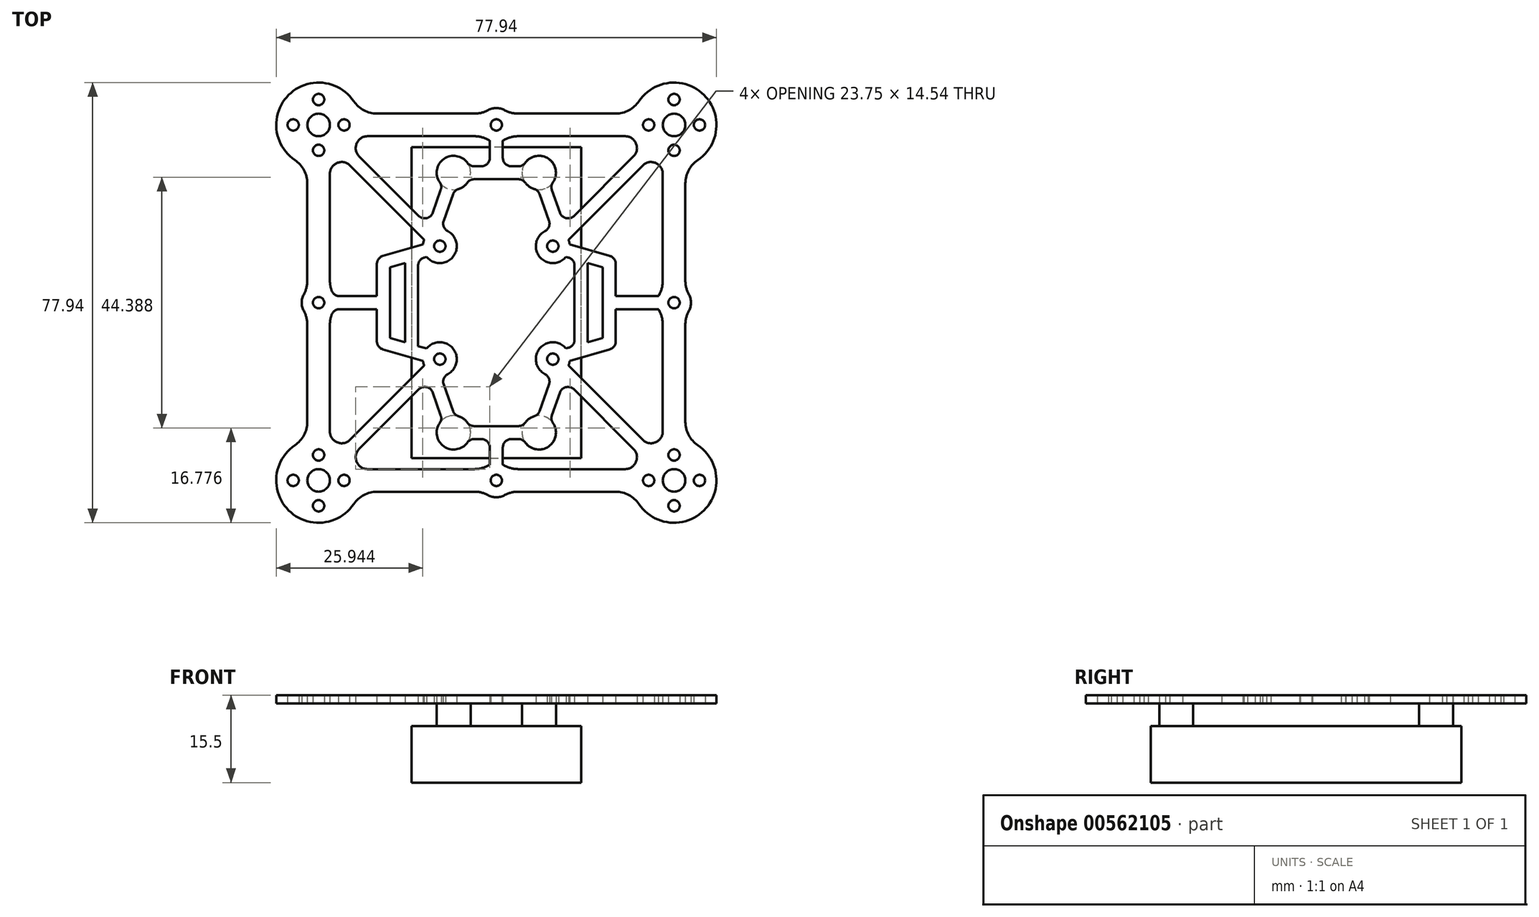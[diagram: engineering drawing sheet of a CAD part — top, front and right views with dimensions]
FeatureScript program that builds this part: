
annotation { "Feature Type Name" : "Feature", "Feature Type Description" : "" }
export const myFeature = defineFeature(function(context is Context, id is Id, definition is map)
    precondition{}
    {
        {
            var Q0;
            Q0=qCreatedBy(makeId("Top.planeOp"),FACE);
            var sketch = newSketch(context, id + "F0", { "sketchPlane" : qUnion([Q0])});
            skLineSegment(sketch, "E0.bottom", {"start": v(15, -27.5) * mm, "end": v(-15, -27.5) * mm});
            skLineSegment(sketch, "E0.top", {"start": v(15, 27.5) * mm, "end": v(-15, 27.5) * mm});
            skLineSegment(sketch, "E0.left", {"start": v(15, -27.5) * mm, "end": v(15, 27.5) * mm});
            skLineSegment(sketch, "E0.right", {"start": v(-15, -27.5) * mm, "end": v(-15, 27.5) * mm});
            skPoint(sketch, "E0.middle", {"position": v(0, 0) * mm});
            skSolve(sketch);
        }
        {
            var Q0;
            Q0=qCreatedBy(makeId("Top.planeOp"),FACE);
            var sketch = newSketch(context, id + "F1", { "sketchPlane" : qUnion([Q0])});
            skCircle(sketch, "E1", {"center": v(0, 0) * mm, "radius": 44.5 * mm, "construction": true});
            skLineSegment(sketch, "E2.bottom", {"start": v(31.47, -31.47) * mm, "end": v(-31.47, -31.47) * mm, "construction": true});
            skLineSegment(sketch, "E2.top", {"start": v(31.47, 31.47) * mm, "end": v(-31.47, 31.47) * mm, "construction": true});
            skLineSegment(sketch, "E2.left", {"start": v(31.47, -31.47) * mm, "end": v(31.47, 31.47) * mm, "construction": true});
            skLineSegment(sketch, "E2.right", {"start": v(-31.47, -31.47) * mm, "end": v(-31.47, 31.47) * mm, "construction": true});
            skCircle(sketch, "E3", {"center": v(-31.47, 31.47) * mm, "radius": 2 * mm});
            skCircle(sketch, "E4", {"center": v(31.47, 31.47) * mm, "radius": 2 * mm});
            skCircle(sketch, "E5", {"center": v(31.47, -31.47) * mm, "radius": 2 * mm});
            skCircle(sketch, "E6", {"center": v(-31.47, -31.47) * mm, "radius": 2 * mm});
            skCircle(sketch, "E7", {"center": v(-31.47, 0) * mm, "radius": 1 * mm});
            skCircle(sketch, "E8", {"center": v(0, 31.47) * mm, "radius": 1 * mm});
            skCircle(sketch, "E9", {"center": v(31.47, 0) * mm, "radius": 1 * mm});
            skCircle(sketch, "E10", {"center": v(0, -31.47) * mm, "radius": 1 * mm});
            skArc(sketch, "E11", {"start": v(-28.3, 24.66) * mm, "mid": v(-28.26, 24.68) * mm, "end": v(-28.22, 24.7) * mm});
            skArc(sketch, "E12", {"start": v(24.66, 28.3) * mm, "mid": v(24.68, 28.26) * mm, "end": v(24.7, 28.22) * mm});
            skArc(sketch, "E13", {"start": v(28.3, -24.66) * mm, "mid": v(28.26, -24.68) * mm, "end": v(28.22, -24.7) * mm});
            skArc(sketch, "E14", {"start": v(-35.67, -25.25) * mm, "mid": v(-36.77, -36.77) * mm, "end": v(-25.25, -35.67) * mm});
            skLineSegment(sketch, "E15.bottom", {"start": v(22.85, -29.47) * mm, "end": v(3.87, -29.47) * mm});
            skLineSegment(sketch, "E15.top", {"start": v(22.85, 29.47) * mm, "end": v(3.87, 29.47) * mm});
            skLineSegment(sketch, "E15.left", {"start": v(29.47, -22.85) * mm, "end": v(29.47, -3.87) * mm});
            skLineSegment(sketch, "E15.right", {"start": v(-29.47, -22.85) * mm, "end": v(-29.47, -3.87) * mm});
            skLineSegment(sketch, "E16.bottom", {"start": v(10, -10) * mm, "end": v(-10, -10) * mm, "construction": true});
            skLineSegment(sketch, "E16.top", {"start": v(10, 10) * mm, "end": v(-10, 10) * mm, "construction": true});
            skLineSegment(sketch, "E16.left", {"start": v(10, -10) * mm, "end": v(10, 10) * mm, "construction": true});
            skLineSegment(sketch, "E16.right", {"start": v(-10, -10) * mm, "end": v(-10, 10) * mm, "construction": true});
            skCircle(sketch, "E17", {"center": v(-10, 10) * mm, "radius": 1 * mm});
            skCircle(sketch, "E18", {"center": v(10, 10) * mm, "radius": 1 * mm});
            skCircle(sketch, "E19", {"center": v(10, -10) * mm, "radius": 1 * mm});
            skCircle(sketch, "E20", {"center": v(-10, -10) * mm, "radius": 1 * mm});
            skLineSegment(sketch, "E21", {"start": v(-31.47, 0) * mm, "end": v(31.47, 0) * mm, "construction": true});
            skLineSegment(sketch, "E22", {"start": v(0, 31.47) * mm, "end": v(0, -31.47) * mm, "construction": true});
            skLineSegment(sketch, "E23.trimOffspring", {"start": v(-33.47, -21.11) * mm, "end": v(-33.47, -3.87) * mm});
            skLineSegment(sketch, "E24.trimOffspring", {"start": v(21.11, 33.47) * mm, "end": v(3.87, 33.47) * mm});
            skLineSegment(sketch, "E25.trimOffspring", {"start": v(21.11, -33.47) * mm, "end": v(3.87, -33.47) * mm});
            skLineSegment(sketch, "E26.trimOffspring", {"start": v(33.47, -21.11) * mm, "end": v(33.47, -3.87) * mm});
            skArc(sketch, "E27.trimOffspring", {"start": v(-25.25, 35.67) * mm, "mid": v(-36.77, 36.77) * mm, "end": v(-35.67, 25.25) * mm});
            skArc(sketch, "E28.trimOffspring", {"start": v(35.67, 25.25) * mm, "mid": v(36.77, 36.77) * mm, "end": v(25.25, 35.67) * mm});
            skArc(sketch, "E29.trimOffspring", {"start": v(25.25, -35.67) * mm, "mid": v(36.77, -36.77) * mm, "end": v(35.67, -25.25) * mm});
            skArc(sketch, "E30.trimOffspring", {"start": v(-24.66, -28.3) * mm, "mid": v(-24.68, -28.26) * mm, "end": v(-24.7, -28.22) * mm});
            skCircle(sketch, "E31", {"center": v(-31.47, 31.47) * mm, "radius": 4.5 * mm, "construction": true});
            skCircle(sketch, "E32", {"center": v(31.47, 31.47) * mm, "radius": 4.5 * mm, "construction": true});
            skCircle(sketch, "E33", {"center": v(31.47, -31.47) * mm, "radius": 4.5 * mm, "construction": true});
            skCircle(sketch, "E34", {"center": v(-31.47, -31.47) * mm, "radius": 4.5 * mm, "construction": true});
            skCircle(sketch, "E35", {"center": v(-26.97, 31.47) * mm, "radius": 1 * mm});
            skCircle(sketch, "E36", {"center": v(-35.97, 31.47) * mm, "radius": 1 * mm});
            skCircle(sketch, "E37", {"center": v(-31.47, 26.97) * mm, "radius": 1 * mm});
            skCircle(sketch, "E38", {"center": v(-31.47, 35.97) * mm, "radius": 1 * mm});
            skCircle(sketch, "E39", {"center": v(26.97, 31.47) * mm, "radius": 1 * mm});
            skCircle(sketch, "E40", {"center": v(31.47, 26.97) * mm, "radius": 1 * mm});
            skCircle(sketch, "E41", {"center": v(31.47, 35.97) * mm, "radius": 1 * mm});
            skCircle(sketch, "E42", {"center": v(35.97, 31.47) * mm, "radius": 1 * mm});
            skCircle(sketch, "E43", {"center": v(31.47, -26.97) * mm, "radius": 1 * mm});
            skCircle(sketch, "E44", {"center": v(26.97, -31.47) * mm, "radius": 1 * mm});
            skCircle(sketch, "E45", {"center": v(35.97, -31.47) * mm, "radius": 1 * mm});
            skCircle(sketch, "E46", {"center": v(31.47, -35.97) * mm, "radius": 1 * mm});
            skCircle(sketch, "E47", {"center": v(-31.47, -26.97) * mm, "radius": 1 * mm});
            skCircle(sketch, "E48", {"center": v(-26.97, -31.47) * mm, "radius": 1 * mm});
            skCircle(sketch, "E49", {"center": v(-31.47, -35.97) * mm, "radius": 1 * mm});
            skCircle(sketch, "E50", {"center": v(-35.97, -31.47) * mm, "radius": 1 * mm});
            skArc(sketch, "E51", {"start": v(-1.45, 28.84) * mm, "mid": v(-1.3, 28.76) * mm, "end": v(-1.15, 28.7) * mm});
            skArc(sketch, "E52", {"start": v(-34.1, 1.45) * mm, "mid": v(-34.47, 0) * mm, "end": v(-34.1, -1.45) * mm});
            skArc(sketch, "E53", {"start": v(28.84, 1.45) * mm, "mid": v(28.76, 1.3) * mm, "end": v(28.7, 1.15) * mm});
            skArc(sketch, "E54", {"start": v(-1.45, -34.1) * mm, "mid": v(0, -34.47) * mm, "end": v(1.45, -34.1) * mm});
            skLineSegment(sketch, "E55.trimOffspring", {"start": v(-3.87, 33.47) * mm, "end": v(-21.11, 33.47) * mm});
            skLineSegment(sketch, "E56.trimOffspring", {"start": v(-3.87, 29.47) * mm, "end": v(-22.85, 29.47) * mm});
            skArc(sketch, "E57.trimOffspring", {"start": v(1.45, 34.1) * mm, "mid": v(0, 34.47) * mm, "end": v(-1.45, 34.1) * mm});
            skLineSegment(sketch, "E58.trimOffspring", {"start": v(-33.47, 3.87) * mm, "end": v(-33.47, 21.11) * mm});
            skLineSegment(sketch, "E59.trimOffspring", {"start": v(-29.47, 3.87) * mm, "end": v(-29.47, 22.85) * mm});
            skLineSegment(sketch, "E60.trimOffspring", {"start": v(-3.87, -29.47) * mm, "end": v(-22.85, -29.47) * mm});
            skArc(sketch, "E61.trimOffspring", {"start": v(1.45, -28.84) * mm, "mid": v(1.3, -28.76) * mm, "end": v(1.15, -28.7) * mm});
            skLineSegment(sketch, "E62.trimOffspring", {"start": v(-3.87, -33.47) * mm, "end": v(-21.11, -33.47) * mm});
            skLineSegment(sketch, "E63.trimOffspring", {"start": v(33.47, 3.87) * mm, "end": v(33.47, 21.11) * mm});
            skLineSegment(sketch, "E64.trimOffspring", {"start": v(29.47, 3.87) * mm, "end": v(29.47, 22.85) * mm});
            skArc(sketch, "E65.trimOffspring", {"start": v(34.1, -1.45) * mm, "mid": v(34.47, 0) * mm, "end": v(34.1, 1.45) * mm});
            skLineSegment(sketch, "E66", {"start": v(-31.47, -31.47) * mm, "end": v(31.47, 31.47) * mm, "construction": true});
            skLineSegment(sketch, "E67", {"start": v(-31.47, 31.47) * mm, "end": v(31.47, -31.47) * mm, "construction": true});
            skArc(sketch, "E68", {"start": v(-12.77, 11.15) * mm, "mid": v(-12.9, 10.75) * mm, "end": v(-12.98, 10.33) * mm});
            skArc(sketch, "E69", {"start": v(8.6, 12.66) * mm, "mid": v(7.68, 8.1) * mm, "end": v(12.34, 8.12) * mm});
            skArc(sketch, "E70", {"start": v(12.77, -11.15) * mm, "mid": v(12.9, -10.75) * mm, "end": v(12.98, -10.33) * mm});
            skArc(sketch, "E71", {"start": v(-8.6, -12.66) * mm, "mid": v(-7.68, -8.1) * mm, "end": v(-12.34, -8.12) * mm});
            skLineSegment(sketch, "E72", {"start": v(-25.94, 24.32) * mm, "end": v(-12.77, 11.15) * mm});
            skLineSegment(sketch, "E73", {"start": v(-24.32, 25.94) * mm, "end": v(-13.73, 15.36) * mm});
            skLineSegment(sketch, "E74", {"start": v(24.32, 25.94) * mm, "end": v(13.73, 15.36) * mm});
            skLineSegment(sketch, "E75", {"start": v(25.94, 24.32) * mm, "end": v(12.77, 11.15) * mm});
            skLineSegment(sketch, "E76", {"start": v(25.94, -24.32) * mm, "end": v(12.77, -11.15) * mm});
            skLineSegment(sketch, "E77", {"start": v(13.73, -15.36) * mm, "end": v(24.32, -25.94) * mm});
            skLineSegment(sketch, "E78", {"start": v(-13.73, -15.36) * mm, "end": v(-24.32, -25.94) * mm});
            skLineSegment(sketch, "E79", {"start": v(-12.77, -11.15) * mm, "end": v(-25.94, -24.32) * mm});
            skPoint(sketch, "E80.visualSharp", {"position": v(-33.47, 24.24) * mm});
            skArc(sketch, "E80.filletArc", {"start": v(-33.47, 21.11) * mm, "mid": v(-34.05, 23.46) * mm, "end": v(-35.67, 25.25) * mm});
            skPoint(sketch, "E81.visualSharp", {"position": v(-24.24, 33.47) * mm});
            skArc(sketch, "E81.filletArc", {"start": v(-25.25, 35.67) * mm, "mid": v(-23.46, 34.05) * mm, "end": v(-21.11, 33.47) * mm});
            skPoint(sketch, "E82.visualSharp", {"position": v(24.24, 33.47) * mm});
            skArc(sketch, "E82.filletArc", {"start": v(21.11, 33.47) * mm, "mid": v(23.46, 34.05) * mm, "end": v(25.25, 35.67) * mm});
            skPoint(sketch, "E83.visualSharp", {"position": v(33.47, 24.24) * mm});
            skArc(sketch, "E83.filletArc", {"start": v(35.67, 25.25) * mm, "mid": v(34.05, 23.46) * mm, "end": v(33.47, 21.11) * mm});
            skPoint(sketch, "E84.visualSharp", {"position": v(33.47, -24.24) * mm});
            skArc(sketch, "E84.filletArc", {"start": v(33.47, -21.11) * mm, "mid": v(34.05, -23.46) * mm, "end": v(35.67, -25.25) * mm});
            skPoint(sketch, "E85.visualSharp", {"position": v(24.24, -33.47) * mm});
            skArc(sketch, "E85.filletArc", {"start": v(25.25, -35.67) * mm, "mid": v(23.46, -34.05) * mm, "end": v(21.11, -33.47) * mm});
            skPoint(sketch, "E86.visualSharp", {"position": v(-33.47, -24.24) * mm});
            skArc(sketch, "E86.filletArc", {"start": v(-35.67, -25.25) * mm, "mid": v(-34.05, -23.46) * mm, "end": v(-33.47, -21.11) * mm});
            skPoint(sketch, "E87.visualSharp", {"position": v(-24.24, -33.47) * mm});
            skArc(sketch, "E87.filletArc", {"start": v(-21.11, -33.47) * mm, "mid": v(-23.46, -34.05) * mm, "end": v(-25.25, -35.67) * mm});
            skPoint(sketch, "E88.visualSharp", {"position": v(-33.47, 2.24) * mm});
            skArc(sketch, "E88.filletArc", {"start": v(-34.1, 1.45) * mm, "mid": v(-33.63, 2.62) * mm, "end": v(-33.47, 3.87) * mm});
            skPoint(sketch, "E89.visualSharp", {"position": v(-33.47, -2.24) * mm});
            skArc(sketch, "E89.filletArc", {"start": v(-33.47, -3.87) * mm, "mid": v(-33.63, -2.62) * mm, "end": v(-34.1, -1.45) * mm});
            skArc(sketch, "E90.filletArc", {"start": v(-29.15, -2.13) * mm, "mid": v(-29.39, -2.99) * mm, "end": v(-29.47, -3.87) * mm});
            skArc(sketch, "E91.filletArc", {"start": v(-29.47, 3.87) * mm, "mid": v(-29.39, 2.99) * mm, "end": v(-29.15, 2.13) * mm});
            skPoint(sketch, "E92.visualSharp", {"position": v(-2.24, 29.47) * mm});
            skArc(sketch, "E92.filletArc", {"start": v(-1.45, 28.84) * mm, "mid": v(-2.62, 29.3) * mm, "end": v(-3.87, 29.47) * mm});
            skPoint(sketch, "E93.visualSharp", {"position": v(2.24, 29.47) * mm});
            skArc(sketch, "E93.filletArc", {"start": v(3.87, 29.47) * mm, "mid": v(2.62, 29.3) * mm, "end": v(1.45, 28.84) * mm});
            skPoint(sketch, "E94.visualSharp", {"position": v(2.24, 33.47) * mm});
            skArc(sketch, "E94.filletArc", {"start": v(1.45, 34.1) * mm, "mid": v(2.62, 33.63) * mm, "end": v(3.87, 33.47) * mm});
            skPoint(sketch, "E95.visualSharp", {"position": v(-2.24, 33.47) * mm});
            skArc(sketch, "E95.filletArc", {"start": v(-3.87, 33.47) * mm, "mid": v(-2.62, 33.63) * mm, "end": v(-1.45, 34.1) * mm});
            skPoint(sketch, "E96.visualSharp", {"position": v(29.47, 2.24) * mm});
            skArc(sketch, "E96.filletArc", {"start": v(28.84, 1.45) * mm, "mid": v(29.3, 2.62) * mm, "end": v(29.47, 3.87) * mm});
            skPoint(sketch, "E97.visualSharp", {"position": v(29.47, -2.24) * mm});
            skArc(sketch, "E97.filletArc", {"start": v(29.47, -3.87) * mm, "mid": v(29.3, -2.62) * mm, "end": v(28.84, -1.45) * mm});
            skPoint(sketch, "E98.visualSharp", {"position": v(33.47, -2.24) * mm});
            skArc(sketch, "E98.filletArc", {"start": v(34.1, -1.45) * mm, "mid": v(33.63, -2.62) * mm, "end": v(33.47, -3.87) * mm});
            skPoint(sketch, "E99.visualSharp", {"position": v(33.47, 2.24) * mm});
            skArc(sketch, "E99.filletArc", {"start": v(33.47, 3.87) * mm, "mid": v(33.63, 2.62) * mm, "end": v(34.1, 1.45) * mm});
            skPoint(sketch, "E100.visualSharp", {"position": v(2.24, -33.47) * mm});
            skArc(sketch, "E100.filletArc", {"start": v(3.87, -33.47) * mm, "mid": v(2.62, -33.63) * mm, "end": v(1.45, -34.1) * mm});
            skPoint(sketch, "E101.visualSharp", {"position": v(-2.24, -33.47) * mm});
            skArc(sketch, "E101.filletArc", {"start": v(-1.45, -34.1) * mm, "mid": v(-2.62, -33.63) * mm, "end": v(-3.87, -33.47) * mm});
            skPoint(sketch, "E102.visualSharp", {"position": v(-2.24, -29.47) * mm});
            skArc(sketch, "E102.filletArc", {"start": v(-3.87, -29.47) * mm, "mid": v(-2.62, -29.3) * mm, "end": v(-1.45, -28.84) * mm});
            skPoint(sketch, "E103.visualSharp", {"position": v(2.24, -29.47) * mm});
            skArc(sketch, "E103.filletArc", {"start": v(1.45, -28.84) * mm, "mid": v(2.62, -29.3) * mm, "end": v(3.87, -29.47) * mm});
            skArc(sketch, "E104.trimOffspring", {"start": v(-24.7, 28.22) * mm, "mid": v(-24.68, 28.26) * mm, "end": v(-24.66, 28.3) * mm});
            skArc(sketch, "E105.trimOffspring", {"start": v(28.22, 24.7) * mm, "mid": v(28.26, 24.68) * mm, "end": v(28.3, 24.66) * mm});
            skArc(sketch, "E106.trimOffspring", {"start": v(-28.22, -24.7) * mm, "mid": v(-28.26, -24.68) * mm, "end": v(-28.3, -24.66) * mm});
            skArc(sketch, "E107.trimOffspring", {"start": v(24.7, -28.22) * mm, "mid": v(24.68, -28.26) * mm, "end": v(24.66, -28.3) * mm});
            skPoint(sketch, "E108.visualSharp", {"position": v(-29.47, 24.24) * mm});
            skArc(sketch, "E108.filletArc", {"start": v(-28.3, 24.66) * mm, "mid": v(-29.15, 23.93) * mm, "end": v(-29.47, 22.85) * mm});
            skPoint(sketch, "E109.visualSharp", {"position": v(-27.04, 25.41) * mm});
            skArc(sketch, "E109.filletArc", {"start": v(-25.94, 24.32) * mm, "mid": v(-27.02, 24.87) * mm, "end": v(-28.22, 24.7) * mm});
            skPoint(sketch, "E110.visualSharp", {"position": v(-24.24, 29.47) * mm});
            skArc(sketch, "E110.filletArc", {"start": v(-22.85, 29.47) * mm, "mid": v(-23.93, 29.15) * mm, "end": v(-24.66, 28.3) * mm});
            skPoint(sketch, "E111.visualSharp", {"position": v(-25.41, 27.04) * mm});
            skArc(sketch, "E111.filletArc", {"start": v(-24.7, 28.22) * mm, "mid": v(-24.87, 27.02) * mm, "end": v(-24.32, 25.94) * mm});
            skPoint(sketch, "E112.visualSharp", {"position": v(24.24, 29.47) * mm});
            skArc(sketch, "E112.filletArc", {"start": v(24.66, 28.3) * mm, "mid": v(23.93, 29.15) * mm, "end": v(22.85, 29.47) * mm});
            skPoint(sketch, "E113.visualSharp", {"position": v(25.41, 27.04) * mm});
            skArc(sketch, "E113.filletArc", {"start": v(24.32, 25.94) * mm, "mid": v(24.87, 27.02) * mm, "end": v(24.7, 28.22) * mm});
            skPoint(sketch, "E114.visualSharp", {"position": v(27.04, 25.41) * mm});
            skArc(sketch, "E114.filletArc", {"start": v(28.22, 24.7) * mm, "mid": v(27.02, 24.87) * mm, "end": v(25.94, 24.32) * mm});
            skPoint(sketch, "E115.visualSharp", {"position": v(29.47, 24.24) * mm});
            skArc(sketch, "E115.filletArc", {"start": v(29.47, 22.85) * mm, "mid": v(29.15, 23.93) * mm, "end": v(28.3, 24.66) * mm});
            skPoint(sketch, "E116.visualSharp", {"position": v(29.47, -24.24) * mm});
            skArc(sketch, "E116.filletArc", {"start": v(28.3, -24.66) * mm, "mid": v(29.15, -23.93) * mm, "end": v(29.47, -22.85) * mm});
            skPoint(sketch, "E117.visualSharp", {"position": v(27.04, -25.41) * mm});
            skArc(sketch, "E117.filletArc", {"start": v(25.94, -24.32) * mm, "mid": v(27.02, -24.87) * mm, "end": v(28.22, -24.7) * mm});
            skPoint(sketch, "E118.visualSharp", {"position": v(25.41, -27.04) * mm});
            skArc(sketch, "E118.filletArc", {"start": v(24.7, -28.22) * mm, "mid": v(24.87, -27.02) * mm, "end": v(24.32, -25.94) * mm});
            skPoint(sketch, "E119.visualSharp", {"position": v(24.24, -29.47) * mm});
            skArc(sketch, "E119.filletArc", {"start": v(22.85, -29.47) * mm, "mid": v(23.93, -29.15) * mm, "end": v(24.66, -28.3) * mm});
            skPoint(sketch, "E120.visualSharp", {"position": v(-24.24, -29.47) * mm});
            skArc(sketch, "E120.filletArc", {"start": v(-24.66, -28.3) * mm, "mid": v(-23.93, -29.15) * mm, "end": v(-22.85, -29.47) * mm});
            skPoint(sketch, "E121.visualSharp", {"position": v(-25.41, -27.04) * mm});
            skArc(sketch, "E121.filletArc", {"start": v(-24.32, -25.94) * mm, "mid": v(-24.87, -27.02) * mm, "end": v(-24.7, -28.22) * mm});
            skPoint(sketch, "E122.visualSharp", {"position": v(-27.04, -25.41) * mm});
            skArc(sketch, "E122.filletArc", {"start": v(-28.22, -24.7) * mm, "mid": v(-27.02, -24.87) * mm, "end": v(-25.94, -24.32) * mm});
            skPoint(sketch, "E123.visualSharp", {"position": v(-29.47, -24.24) * mm});
            skArc(sketch, "E123.filletArc", {"start": v(-29.47, -22.85) * mm, "mid": v(-29.15, -23.93) * mm, "end": v(-28.3, -24.66) * mm});
            skLineSegment(sketch, "E124", {"start": v(-12.88, 9.16) * mm, "end": v(-20, 7.1) * mm, "construction": true});
            skLineSegment(sketch, "E125", {"start": v(-20, 7.1) * mm, "end": v(-20, -7.1) * mm, "construction": true});
            skLineSegment(sketch, "E126", {"start": v(-20, -7.1) * mm, "end": v(-12.88, -9.16) * mm, "construction": true});
            skLineSegment(sketch, "E127", {"start": v(20, 7.1) * mm, "end": v(20, -7.1) * mm, "construction": true});
            skLineSegment(sketch, "E128", {"start": v(-11.15, 12.77) * mm, "end": v(-7.55, 23) * mm, "construction": true});
            skLineSegment(sketch, "E129", {"start": v(-7.55, 23) * mm, "end": v(7.55, 23) * mm, "construction": true});
            skLineSegment(sketch, "E130", {"start": v(7.55, 23) * mm, "end": v(11.15, 12.77) * mm, "construction": true});
            skLineSegment(sketch, "E131", {"start": v(-11.15, -12.77) * mm, "end": v(-7.55, -23) * mm, "construction": true});
            skLineSegment(sketch, "E132", {"start": v(-7.55, -23) * mm, "end": v(7.55, -23) * mm, "construction": true});
            skLineSegment(sketch, "E133", {"start": v(7.55, -23) * mm, "end": v(11.15, -12.77) * mm, "construction": true});
            skPoint(sketch, "E134", {"position": v(0, 23) * mm});
            skPoint(sketch, "E135", {"position": v(0, -23) * mm});
            skPoint(sketch, "E136", {"position": v(-20, 0) * mm});
            skPoint(sketch, "E137", {"position": v(20, 0) * mm});
            skPoint(sketch, "E138", {"position": v(0, -44.5) * mm});
            skPoint(sketch, "E139", {"position": v(-44.5, 0) * mm});
            skLineSegment(sketch, "E140", {"start": v(20, 7.1) * mm, "end": v(12.88, 9.16) * mm, "construction": true});
            skLineSegment(sketch, "E141", {"start": v(20, -7.1) * mm, "end": v(12.88, -9.16) * mm, "construction": true});
            skArc(sketch, "E142", {"start": v(-6.69, 20.13) * mm, "mid": v(-5.82, 20.55) * mm, "end": v(-5.13, 21.23) * mm});
            skArc(sketch, "E143", {"start": v(-10.02, -21.3) * mm, "mid": v(-9.29, -25.45) * mm, "end": v(-5.13, -24.77) * mm});
            skArc(sketch, "E144", {"start": v(5.13, -24.77) * mm, "mid": v(9.29, -25.45) * mm, "end": v(10.02, -21.3) * mm});
            skLineSegment(sketch, "E145", {"start": v(-9.84, 19.95) * mm, "end": v(-11.26, 15.92) * mm});
            skLineSegment(sketch, "E146", {"start": v(-7.67, 19.19) * mm, "end": v(-9.33, 14.48) * mm});
            skLineSegment(sketch, "E147", {"start": v(7.67, 19.19) * mm, "end": v(9.33, 14.48) * mm});
            skLineSegment(sketch, "E148", {"start": v(9.84, 19.95) * mm, "end": v(11.26, 15.92) * mm});
            skLineSegment(sketch, "E149", {"start": v(11.26, -15.92) * mm, "end": v(9.84, -19.95) * mm});
            skLineSegment(sketch, "E150", {"start": v(9.33, -14.48) * mm, "end": v(7.67, -19.19) * mm});
            skLineSegment(sketch, "E151", {"start": v(3.92, -21.85) * mm, "end": v(-3.92, -21.85) * mm});
            skLineSegment(sketch, "E152", {"start": v(-3.92, -24.15) * mm, "end": v(-2.65, -24.15) * mm});
            skLineSegment(sketch, "E153", {"start": v(-9.84, -19.95) * mm, "end": v(-11.26, -15.92) * mm});
            skLineSegment(sketch, "E154", {"start": v(-7.67, -19.19) * mm, "end": v(-9.33, -14.48) * mm});
            skLineSegment(sketch, "E155", {"start": v(-3.92, 21.85) * mm, "end": v(3.92, 21.85) * mm});
            skLineSegment(sketch, "E156", {"start": v(3.92, 24.15) * mm, "end": v(2.65, 24.15) * mm});
            skLineSegment(sketch, "E157", {"start": v(-1.15, 28.7) * mm, "end": v(-1.15, 25.65) * mm});
            skLineSegment(sketch, "E158", {"start": v(1.15, 28.7) * mm, "end": v(1.15, 25.65) * mm});
            skLineSegment(sketch, "E159", {"start": v(-1.15, -25.65) * mm, "end": v(-1.15, -28.7) * mm});
            skLineSegment(sketch, "E160", {"start": v(1.15, -25.65) * mm, "end": v(1.15, -28.7) * mm});
            skArc(sketch, "E161.trimOffspring", {"start": v(-5.13, 24.77) * mm, "mid": v(-9.29, 25.45) * mm, "end": v(-10.02, 21.3) * mm});
            skLineSegment(sketch, "E162.trimOffspring", {"start": v(-2.65, 24.15) * mm, "end": v(-3.92, 24.15) * mm});
            skArc(sketch, "E163.trimOffspring", {"start": v(10.02, 21.3) * mm, "mid": v(9.29, 25.45) * mm, "end": v(5.13, 24.77) * mm});
            skArc(sketch, "E164", {"start": v(5.13, 21.23) * mm, "mid": v(5.82, 20.55) * mm, "end": v(6.69, 20.13) * mm});
            skArc(sketch, "E165.trimOffspring", {"start": v(-5.13, -21.23) * mm, "mid": v(-5.82, -20.55) * mm, "end": v(-6.69, -20.13) * mm});
            skLineSegment(sketch, "E166.trimOffspring", {"start": v(2.65, -24.15) * mm, "end": v(3.92, -24.15) * mm});
            skArc(sketch, "E167.trimOffspring", {"start": v(6.69, -20.13) * mm, "mid": v(5.82, -20.55) * mm, "end": v(5.13, -21.23) * mm});
            skArc(sketch, "E168.trimOffspring", {"start": v(1.15, 28.7) * mm, "mid": v(1.3, 28.76) * mm, "end": v(1.45, 28.84) * mm});
            skArc(sketch, "E169.trimOffspring", {"start": v(-1.15, -28.7) * mm, "mid": v(-1.3, -28.76) * mm, "end": v(-1.45, -28.84) * mm});
            skLineSegment(sketch, "E170", {"start": v(-15, 8.55) * mm, "end": v(-15, -8.55) * mm, "construction": true});
            skLineSegment(sketch, "E171", {"start": v(15, 8.55) * mm, "end": v(15, -8.55) * mm, "construction": true});
            skLineSegment(sketch, "E172", {"start": v(-27.75, 1.15) * mm, "end": v(-21.15, 1.15) * mm});
            skLineSegment(sketch, "E173", {"start": v(-21.15, 1.15) * mm, "end": v(-21.15, 6.84) * mm});
            skLineSegment(sketch, "E174", {"start": v(-20.07, 8.28) * mm, "end": v(-12.98, 10.33) * mm});
            skLineSegment(sketch, "E175", {"start": v(-27.75, -1.15) * mm, "end": v(-21.15, -1.15) * mm});
            skLineSegment(sketch, "E176", {"start": v(-21.15, -1.15) * mm, "end": v(-21.15, -6.84) * mm});
            skLineSegment(sketch, "E177", {"start": v(-20.07, -8.28) * mm, "end": v(-12.98, -10.33) * mm});
            skLineSegment(sketch, "E178", {"start": v(-12.34, 8.12) * mm, "end": v(-12.77, 8) * mm});
            skLineSegment(sketch, "E179", {"start": v(-13.85, 6.56) * mm, "end": v(-13.85, -7.69) * mm});
            skLineSegment(sketch, "E180", {"start": v(-13.85, -7.69) * mm, "end": v(-12.34, -8.12) * mm});
            skLineSegment(sketch, "E181", {"start": v(-16.15, 7.02) * mm, "end": v(-18.85, 6.24) * mm});
            skLineSegment(sketch, "E182", {"start": v(-18.85, 6.24) * mm, "end": v(-18.85, -6.24) * mm});
            skLineSegment(sketch, "E183", {"start": v(-18.85, -6.24) * mm, "end": v(-16.15, -7.02) * mm});
            skLineSegment(sketch, "E184", {"start": v(-16.15, -7.02) * mm, "end": v(-16.15, 7.02) * mm});
            skArc(sketch, "E185.trimOffspring", {"start": v(-12.34, 8.12) * mm, "mid": v(-7.68, 8.1) * mm, "end": v(-8.6, 12.66) * mm});
            skArc(sketch, "E186.trimOffspring", {"start": v(-12.98, -10.33) * mm, "mid": v(-12.9, -10.75) * mm, "end": v(-12.77, -11.15) * mm});
            skLineSegment(sketch, "E187", {"start": v(28.7, 1.15) * mm, "end": v(21.15, 1.15) * mm});
            skLineSegment(sketch, "E188", {"start": v(21.15, 1.15) * mm, "end": v(21.15, 6.84) * mm});
            skLineSegment(sketch, "E189", {"start": v(20.07, 8.28) * mm, "end": v(12.98, 10.33) * mm});
            skLineSegment(sketch, "E190", {"start": v(28.7, -1.15) * mm, "end": v(21.15, -1.15) * mm});
            skLineSegment(sketch, "E191", {"start": v(21.15, -1.15) * mm, "end": v(21.15, -6.84) * mm});
            skLineSegment(sketch, "E192", {"start": v(20.07, -8.28) * mm, "end": v(12.98, -10.33) * mm});
            skLineSegment(sketch, "E193", {"start": v(12.34, -8.12) * mm, "end": v(12.77, -8) * mm});
            skLineSegment(sketch, "E194", {"start": v(13.85, -6.56) * mm, "end": v(13.85, 6.56) * mm});
            skLineSegment(sketch, "E195", {"start": v(12.77, 8) * mm, "end": v(12.34, 8.12) * mm});
            skLineSegment(sketch, "E196", {"start": v(16.15, 7.02) * mm, "end": v(18.85, 6.24) * mm});
            skLineSegment(sketch, "E197", {"start": v(18.85, 6.24) * mm, "end": v(18.85, -6.24) * mm});
            skLineSegment(sketch, "E198", {"start": v(18.85, -6.24) * mm, "end": v(16.15, -7.02) * mm});
            skLineSegment(sketch, "E199", {"start": v(16.15, -7.02) * mm, "end": v(16.15, 7.02) * mm});
            skArc(sketch, "E200.trimOffspring", {"start": v(12.98, 10.33) * mm, "mid": v(12.9, 10.75) * mm, "end": v(12.77, 11.15) * mm});
            skArc(sketch, "E201.trimOffspring", {"start": v(28.7, -1.15) * mm, "mid": v(28.76, -1.3) * mm, "end": v(28.84, -1.45) * mm});
            skArc(sketch, "E202.trimOffspring", {"start": v(12.34, -8.12) * mm, "mid": v(7.68, -8.1) * mm, "end": v(8.6, -12.66) * mm});
            skPoint(sketch, "E203.visualSharp", {"position": v(-9.56, 20.77) * mm});
            skArc(sketch, "E203.filletArc", {"start": v(-9.84, 19.95) * mm, "mid": v(-9.77, 20.65) * mm, "end": v(-10.02, 21.3) * mm});
            skPoint(sketch, "E204.visualSharp", {"position": v(-4.78, 24.15) * mm});
            skArc(sketch, "E204.filletArc", {"start": v(-5.13, 24.77) * mm, "mid": v(-4.6, 24.31) * mm, "end": v(-3.92, 24.15) * mm});
            skPoint(sketch, "E205.visualSharp", {"position": v(-7.39, 20) * mm});
            skArc(sketch, "E205.filletArc", {"start": v(-6.69, 20.13) * mm, "mid": v(-7.3, 19.78) * mm, "end": v(-7.67, 19.19) * mm});
            skPoint(sketch, "E206.visualSharp", {"position": v(-4.78, 21.85) * mm});
            skArc(sketch, "E206.filletArc", {"start": v(-3.92, 21.85) * mm, "mid": v(-4.6, 21.69) * mm, "end": v(-5.13, 21.23) * mm});
            skPoint(sketch, "E207.visualSharp", {"position": v(4.78, 21.85) * mm});
            skArc(sketch, "E207.filletArc", {"start": v(5.13, 21.23) * mm, "mid": v(4.6, 21.69) * mm, "end": v(3.92, 21.85) * mm});
            skPoint(sketch, "E208.visualSharp", {"position": v(4.78, 24.15) * mm});
            skArc(sketch, "E208.filletArc", {"start": v(3.92, 24.15) * mm, "mid": v(4.6, 24.31) * mm, "end": v(5.13, 24.77) * mm});
            skPoint(sketch, "E209.visualSharp", {"position": v(9.56, 20.77) * mm});
            skArc(sketch, "E209.filletArc", {"start": v(10.02, 21.3) * mm, "mid": v(9.77, 20.65) * mm, "end": v(9.84, 19.95) * mm});
            skPoint(sketch, "E210.visualSharp", {"position": v(7.39, 20) * mm});
            skArc(sketch, "E210.filletArc", {"start": v(7.67, 19.19) * mm, "mid": v(7.3, 19.78) * mm, "end": v(6.69, 20.13) * mm});
            skPoint(sketch, "E211.visualSharp", {"position": v(-9.56, -20.77) * mm});
            skArc(sketch, "E211.filletArc", {"start": v(-10.02, -21.3) * mm, "mid": v(-9.77, -20.65) * mm, "end": v(-9.84, -19.95) * mm});
            skPoint(sketch, "E212.visualSharp", {"position": v(-7.39, -20) * mm});
            skArc(sketch, "E212.filletArc", {"start": v(-7.67, -19.19) * mm, "mid": v(-7.3, -19.78) * mm, "end": v(-6.69, -20.13) * mm});
            skPoint(sketch, "E213.visualSharp", {"position": v(-4.78, -21.85) * mm});
            skArc(sketch, "E213.filletArc", {"start": v(-5.13, -21.23) * mm, "mid": v(-4.6, -21.69) * mm, "end": v(-3.92, -21.85) * mm});
            skPoint(sketch, "E214.visualSharp", {"position": v(-4.78, -24.15) * mm});
            skArc(sketch, "E214.filletArc", {"start": v(-3.92, -24.15) * mm, "mid": v(-4.6, -24.31) * mm, "end": v(-5.13, -24.77) * mm});
            skPoint(sketch, "E215.visualSharp", {"position": v(4.78, -21.85) * mm});
            skArc(sketch, "E215.filletArc", {"start": v(3.92, -21.85) * mm, "mid": v(4.6, -21.69) * mm, "end": v(5.13, -21.23) * mm});
            skPoint(sketch, "E216.visualSharp", {"position": v(4.78, -24.15) * mm});
            skArc(sketch, "E216.filletArc", {"start": v(5.13, -24.77) * mm, "mid": v(4.6, -24.31) * mm, "end": v(3.92, -24.15) * mm});
            skPoint(sketch, "E217.visualSharp", {"position": v(7.39, -20) * mm});
            skArc(sketch, "E217.filletArc", {"start": v(6.69, -20.13) * mm, "mid": v(7.3, -19.78) * mm, "end": v(7.67, -19.19) * mm});
            skPoint(sketch, "E218.visualSharp", {"position": v(9.56, -20.77) * mm});
            skArc(sketch, "E218.filletArc", {"start": v(9.84, -19.95) * mm, "mid": v(9.77, -20.65) * mm, "end": v(10.02, -21.3) * mm});
            skPoint(sketch, "E219.visualSharp", {"position": v(1.15, -24.15) * mm});
            skArc(sketch, "E219.filletArc", {"start": v(2.65, -24.15) * mm, "mid": v(1.59, -24.59) * mm, "end": v(1.15, -25.65) * mm});
            skPoint(sketch, "E220.visualSharp", {"position": v(-1.15, -24.15) * mm});
            skArc(sketch, "E220.filletArc", {"start": v(-1.15, -25.65) * mm, "mid": v(-1.59, -24.59) * mm, "end": v(-2.65, -24.15) * mm});
            skPoint(sketch, "E221.visualSharp", {"position": v(-1.15, 24.15) * mm});
            skArc(sketch, "E221.filletArc", {"start": v(-2.65, 24.15) * mm, "mid": v(-1.59, 24.59) * mm, "end": v(-1.15, 25.65) * mm});
            skPoint(sketch, "E222.visualSharp", {"position": v(1.15, 24.15) * mm});
            skArc(sketch, "E222.filletArc", {"start": v(1.15, 25.65) * mm, "mid": v(1.59, 24.59) * mm, "end": v(2.65, 24.15) * mm});
            skPoint(sketch, "E223.visualSharp", {"position": v(-9.85, 13) * mm});
            skArc(sketch, "E223.filletArc", {"start": v(-9.33, 14.48) * mm, "mid": v(-9.3, 13.44) * mm, "end": v(-8.6, 12.66) * mm});
            skPoint(sketch, "E224.visualSharp", {"position": v(9.85, 13) * mm});
            skArc(sketch, "E224.filletArc", {"start": v(8.6, 12.66) * mm, "mid": v(9.3, 13.44) * mm, "end": v(9.33, 14.48) * mm});
            skPoint(sketch, "E225.visualSharp", {"position": v(12.05, 13.67) * mm});
            skArc(sketch, "E225.filletArc", {"start": v(11.26, 15.92) * mm, "mid": v(12.34, 14.96) * mm, "end": v(13.73, 15.36) * mm});
            skPoint(sketch, "E226.visualSharp", {"position": v(-12.05, 13.67) * mm});
            skArc(sketch, "E226.filletArc", {"start": v(-13.73, 15.36) * mm, "mid": v(-12.34, 14.96) * mm, "end": v(-11.26, 15.92) * mm});
            skPoint(sketch, "E227.visualSharp", {"position": v(-12.05, -13.67) * mm});
            skArc(sketch, "E227.filletArc", {"start": v(-11.26, -15.92) * mm, "mid": v(-12.34, -14.96) * mm, "end": v(-13.73, -15.36) * mm});
            skPoint(sketch, "E228.visualSharp", {"position": v(12.05, -13.67) * mm});
            skArc(sketch, "E228.filletArc", {"start": v(13.73, -15.36) * mm, "mid": v(12.34, -14.96) * mm, "end": v(11.26, -15.92) * mm});
            skPoint(sketch, "E229.visualSharp", {"position": v(-9.85, -13) * mm});
            skArc(sketch, "E229.filletArc", {"start": v(-8.6, -12.66) * mm, "mid": v(-9.3, -13.44) * mm, "end": v(-9.33, -14.48) * mm});
            skPoint(sketch, "E230.visualSharp", {"position": v(9.85, -13) * mm});
            skArc(sketch, "E230.filletArc", {"start": v(9.33, -14.48) * mm, "mid": v(9.3, -13.44) * mm, "end": v(8.6, -12.66) * mm});
            skPoint(sketch, "E231.visualSharp", {"position": v(-21.15, 7.97) * mm});
            skArc(sketch, "E231.filletArc", {"start": v(-20.07, 8.28) * mm, "mid": v(-20.85, 7.74) * mm, "end": v(-21.15, 6.84) * mm});
            skPoint(sketch, "E232.visualSharp", {"position": v(-21.15, -7.97) * mm});
            skArc(sketch, "E232.filletArc", {"start": v(-21.15, -6.84) * mm, "mid": v(-20.85, -7.74) * mm, "end": v(-20.07, -8.28) * mm});
            skPoint(sketch, "E233.visualSharp", {"position": v(21.15, -7.97) * mm});
            skArc(sketch, "E233.filletArc", {"start": v(20.07, -8.28) * mm, "mid": v(20.85, -7.74) * mm, "end": v(21.15, -6.84) * mm});
            skPoint(sketch, "E234.visualSharp", {"position": v(21.15, 7.97) * mm});
            skArc(sketch, "E234.filletArc", {"start": v(21.15, 6.84) * mm, "mid": v(20.85, 7.74) * mm, "end": v(20.07, 8.28) * mm});
            skPoint(sketch, "E235.visualSharp", {"position": v(13.85, 7.69) * mm});
            skArc(sketch, "E235.filletArc", {"start": v(13.85, 6.56) * mm, "mid": v(13.55, 7.46) * mm, "end": v(12.77, 8) * mm});
            skPoint(sketch, "E236.visualSharp", {"position": v(13.85, -7.69) * mm});
            skArc(sketch, "E236.filletArc", {"start": v(12.77, -8) * mm, "mid": v(13.55, -7.46) * mm, "end": v(13.85, -6.56) * mm});
            skPoint(sketch, "E237.visualSharp", {"position": v(-13.85, 7.69) * mm});
            skArc(sketch, "E237.filletArc", {"start": v(-12.77, 8) * mm, "mid": v(-13.55, 7.46) * mm, "end": v(-13.85, 6.56) * mm});
            skPoint(sketch, "E238.visualSharp", {"position": v(-28.66, 1.15) * mm});
            skArc(sketch, "E238.filletArc", {"start": v(-29.15, 2.13) * mm, "mid": v(-28.6, 1.42) * mm, "end": v(-27.75, 1.15) * mm});
            skPoint(sketch, "E239.visualSharp", {"position": v(-28.66, -1.15) * mm});
            skArc(sketch, "E239.filletArc", {"start": v(-27.75, -1.15) * mm, "mid": v(-28.6, -1.42) * mm, "end": v(-29.15, -2.13) * mm});
            skSolve(sketch);
        }
        {
            var Q0;
            Q0=makeQuery(id+"F1.imprint","IMPRINT",FACE,{"disambiguationData":[TD([[makeQuery(id+"F1.imprint","IMPRINT",EDGE,{"derivedFrom":sQuery(id+"F1.wireOp",EDGE,"E3")}),-1.0]])]});
            extrude(context, id + "F2", {"entities" : qUnion([Q0]), "depth" : 1.5 * mm, "offsetDistance" : 25 * mm});
        }
        {
            var Q0;
            Q0=makeQuery(id+"F2.opExtrude","CAP_FACE",FACE,{"disambiguationData":[OSD([sQuery(id+"F1.wireOp",EDGE,"E3"),sQuery(id+"F1.wireOp",EDGE,"E4"),sQuery(id+"F1.wireOp",EDGE,"E5"),sQuery(id+"F1.wireOp",EDGE,"E6"),sQuery(id+"F1.wireOp",EDGE,"E7"),sQuery(id+"F1.wireOp",EDGE,"E8"),sQuery(id+"F1.wireOp",EDGE,"E9"),sQuery(id+"F1.wireOp",EDGE,"E10"),sQuery(id+"F1.wireOp",EDGE,"E11"),sQuery(id+"F1.wireOp",EDGE,"E12"),sQuery(id+"F1.wireOp",EDGE,"E13"),sQuery(id+"F1.wireOp",EDGE,"E14"),sQuery(id+"F1.wireOp",EDGE,"E15.bottom"),sQuery(id+"F1.wireOp",EDGE,"E15.top"),sQuery(id+"F1.wireOp",EDGE,"E15.left"),sQuery(id+"F1.wireOp",EDGE,"E15.right"),sQuery(id+"F1.wireOp",EDGE,"E17"),sQuery(id+"F1.wireOp",EDGE,"E18"),sQuery(id+"F1.wireOp",EDGE,"E19"),sQuery(id+"F1.wireOp",EDGE,"E20"),sQuery(id+"F1.wireOp",EDGE,"E23.trimOffspring"),sQuery(id+"F1.wireOp",EDGE,"E24.trimOffspring"),sQuery(id+"F1.wireOp",EDGE,"E25.trimOffspring"),sQuery(id+"F1.wireOp",EDGE,"E26.trimOffspring"),sQuery(id+"F1.wireOp",EDGE,"E27.trimOffspring"),sQuery(id+"F1.wireOp",EDGE,"E28.trimOffspring"),sQuery(id+"F1.wireOp",EDGE,"E29.trimOffspring"),sQuery(id+"F1.wireOp",EDGE,"E30.trimOffspring"),sQuery(id+"F1.wireOp",EDGE,"E35"),sQuery(id+"F1.wireOp",EDGE,"E36"),sQuery(id+"F1.wireOp",EDGE,"E37"),sQuery(id+"F1.wireOp",EDGE,"E38"),sQuery(id+"F1.wireOp",EDGE,"E39"),sQuery(id+"F1.wireOp",EDGE,"E40"),sQuery(id+"F1.wireOp",EDGE,"E41"),sQuery(id+"F1.wireOp",EDGE,"E42"),sQuery(id+"F1.wireOp",EDGE,"E43"),sQuery(id+"F1.wireOp",EDGE,"E44"),sQuery(id+"F1.wireOp",EDGE,"E45"),sQuery(id+"F1.wireOp",EDGE,"E46"),sQuery(id+"F1.wireOp",EDGE,"E47"),sQuery(id+"F1.wireOp",EDGE,"E48"),sQuery(id+"F1.wireOp",EDGE,"E49"),sQuery(id+"F1.wireOp",EDGE,"E50"),sQuery(id+"F1.wireOp",EDGE,"E51"),sQuery(id+"F1.wireOp",EDGE,"E52"),sQuery(id+"F1.wireOp",EDGE,"E53"),sQuery(id+"F1.wireOp",EDGE,"E54"),sQuery(id+"F1.wireOp",EDGE,"E55.trimOffspring"),sQuery(id+"F1.wireOp",EDGE,"E56.trimOffspring"),sQuery(id+"F1.wireOp",EDGE,"E57.trimOffspring"),sQuery(id+"F1.wireOp",EDGE,"E58.trimOffspring"),sQuery(id+"F1.wireOp",EDGE,"E59.trimOffspring"),sQuery(id+"F1.wireOp",EDGE,"E60.trimOffspring"),sQuery(id+"F1.wireOp",EDGE,"E61.trimOffspring"),sQuery(id+"F1.wireOp",EDGE,"E62.trimOffspring"),sQuery(id+"F1.wireOp",EDGE,"E63.trimOffspring"),sQuery(id+"F1.wireOp",EDGE,"E64.trimOffspring"),sQuery(id+"F1.wireOp",EDGE,"E65.trimOffspring"),sQuery(id+"F1.wireOp",EDGE,"E68"),sQuery(id+"F1.wireOp",EDGE,"E69"),sQuery(id+"F1.wireOp",EDGE,"E70"),sQuery(id+"F1.wireOp",EDGE,"E71"),sQuery(id+"F1.wireOp",EDGE,"E72"),sQuery(id+"F1.wireOp",EDGE,"E73"),sQuery(id+"F1.wireOp",EDGE,"E74"),sQuery(id+"F1.wireOp",EDGE,"E75"),sQuery(id+"F1.wireOp",EDGE,"E76"),sQuery(id+"F1.wireOp",EDGE,"E77"),sQuery(id+"F1.wireOp",EDGE,"E78"),sQuery(id+"F1.wireOp",EDGE,"E79"),sQuery(id+"F1.wireOp",EDGE,"E80.filletArc"),sQuery(id+"F1.wireOp",EDGE,"E81.filletArc"),sQuery(id+"F1.wireOp",EDGE,"E82.filletArc"),sQuery(id+"F1.wireOp",EDGE,"E83.filletArc"),sQuery(id+"F1.wireOp",EDGE,"E84.filletArc"),sQuery(id+"F1.wireOp",EDGE,"E85.filletArc"),sQuery(id+"F1.wireOp",EDGE,"E86.filletArc"),sQuery(id+"F1.wireOp",EDGE,"E87.filletArc"),sQuery(id+"F1.wireOp",EDGE,"E88.filletArc"),sQuery(id+"F1.wireOp",EDGE,"E89.filletArc"),sQuery(id+"F1.wireOp",EDGE,"E90.filletArc"),sQuery(id+"F1.wireOp",EDGE,"E91.filletArc"),sQuery(id+"F1.wireOp",EDGE,"E92.filletArc"),sQuery(id+"F1.wireOp",EDGE,"E93.filletArc"),sQuery(id+"F1.wireOp",EDGE,"E94.filletArc"),sQuery(id+"F1.wireOp",EDGE,"E95.filletArc"),sQuery(id+"F1.wireOp",EDGE,"E96.filletArc"),sQuery(id+"F1.wireOp",EDGE,"E97.filletArc"),sQuery(id+"F1.wireOp",EDGE,"E98.filletArc"),sQuery(id+"F1.wireOp",EDGE,"E99.filletArc"),sQuery(id+"F1.wireOp",EDGE,"E100.filletArc"),sQuery(id+"F1.wireOp",EDGE,"E101.filletArc"),sQuery(id+"F1.wireOp",EDGE,"E102.filletArc"),sQuery(id+"F1.wireOp",EDGE,"E103.filletArc"),sQuery(id+"F1.wireOp",EDGE,"E104.trimOffspring"),sQuery(id+"F1.wireOp",EDGE,"E105.trimOffspring"),sQuery(id+"F1.wireOp",EDGE,"E106.trimOffspring"),sQuery(id+"F1.wireOp",EDGE,"E107.trimOffspring"),sQuery(id+"F1.wireOp",EDGE,"E108.filletArc"),sQuery(id+"F1.wireOp",EDGE,"E109.filletArc"),sQuery(id+"F1.wireOp",EDGE,"E110.filletArc"),sQuery(id+"F1.wireOp",EDGE,"E111.filletArc"),sQuery(id+"F1.wireOp",EDGE,"E112.filletArc"),sQuery(id+"F1.wireOp",EDGE,"E113.filletArc"),sQuery(id+"F1.wireOp",EDGE,"E114.filletArc"),sQuery(id+"F1.wireOp",EDGE,"E115.filletArc"),sQuery(id+"F1.wireOp",EDGE,"E116.filletArc"),sQuery(id+"F1.wireOp",EDGE,"E117.filletArc"),sQuery(id+"F1.wireOp",EDGE,"E118.filletArc"),sQuery(id+"F1.wireOp",EDGE,"E119.filletArc"),sQuery(id+"F1.wireOp",EDGE,"E120.filletArc"),sQuery(id+"F1.wireOp",EDGE,"E121.filletArc"),sQuery(id+"F1.wireOp",EDGE,"E122.filletArc"),sQuery(id+"F1.wireOp",EDGE,"E123.filletArc"),sQuery(id+"F1.wireOp",EDGE,"E142"),sQuery(id+"F1.wireOp",EDGE,"E143"),sQuery(id+"F1.wireOp",EDGE,"E144"),sQuery(id+"F1.wireOp",EDGE,"E145"),sQuery(id+"F1.wireOp",EDGE,"E146"),sQuery(id+"F1.wireOp",EDGE,"E147"),sQuery(id+"F1.wireOp",EDGE,"E148"),sQuery(id+"F1.wireOp",EDGE,"E149"),sQuery(id+"F1.wireOp",EDGE,"E150"),sQuery(id+"F1.wireOp",EDGE,"E151"),sQuery(id+"F1.wireOp",EDGE,"E152"),sQuery(id+"F1.wireOp",EDGE,"E153"),sQuery(id+"F1.wireOp",EDGE,"E154"),sQuery(id+"F1.wireOp",EDGE,"E155"),sQuery(id+"F1.wireOp",EDGE,"E156"),sQuery(id+"F1.wireOp",EDGE,"E157"),sQuery(id+"F1.wireOp",EDGE,"E158"),sQuery(id+"F1.wireOp",EDGE,"E159"),sQuery(id+"F1.wireOp",EDGE,"E160"),sQuery(id+"F1.wireOp",EDGE,"E161.trimOffspring"),sQuery(id+"F1.wireOp",EDGE,"E162.trimOffspring"),sQuery(id+"F1.wireOp",EDGE,"E163.trimOffspring"),sQuery(id+"F1.wireOp",EDGE,"E164"),sQuery(id+"F1.wireOp",EDGE,"E165.trimOffspring"),sQuery(id+"F1.wireOp",EDGE,"E166.trimOffspring"),sQuery(id+"F1.wireOp",EDGE,"E167.trimOffspring"),sQuery(id+"F1.wireOp",EDGE,"E168.trimOffspring"),sQuery(id+"F1.wireOp",EDGE,"E169.trimOffspring"),sQuery(id+"F1.wireOp",EDGE,"E172"),sQuery(id+"F1.wireOp",EDGE,"E173"),sQuery(id+"F1.wireOp",EDGE,"E174"),sQuery(id+"F1.wireOp",EDGE,"E175"),sQuery(id+"F1.wireOp",EDGE,"E176"),sQuery(id+"F1.wireOp",EDGE,"E177"),sQuery(id+"F1.wireOp",EDGE,"E178"),sQuery(id+"F1.wireOp",EDGE,"E179"),sQuery(id+"F1.wireOp",EDGE,"E180"),sQuery(id+"F1.wireOp",EDGE,"E181"),sQuery(id+"F1.wireOp",EDGE,"E182"),sQuery(id+"F1.wireOp",EDGE,"E183"),sQuery(id+"F1.wireOp",EDGE,"E184"),sQuery(id+"F1.wireOp",EDGE,"E185.trimOffspring"),sQuery(id+"F1.wireOp",EDGE,"E186.trimOffspring"),sQuery(id+"F1.wireOp",EDGE,"E187"),sQuery(id+"F1.wireOp",EDGE,"E188"),sQuery(id+"F1.wireOp",EDGE,"E189"),sQuery(id+"F1.wireOp",EDGE,"E190"),sQuery(id+"F1.wireOp",EDGE,"E191"),sQuery(id+"F1.wireOp",EDGE,"E192"),sQuery(id+"F1.wireOp",EDGE,"E193"),sQuery(id+"F1.wireOp",EDGE,"E194"),sQuery(id+"F1.wireOp",EDGE,"E195"),sQuery(id+"F1.wireOp",EDGE,"E196"),sQuery(id+"F1.wireOp",EDGE,"E197"),sQuery(id+"F1.wireOp",EDGE,"E198"),sQuery(id+"F1.wireOp",EDGE,"E199"),sQuery(id+"F1.wireOp",EDGE,"E200.trimOffspring"),sQuery(id+"F1.wireOp",EDGE,"E201.trimOffspring"),sQuery(id+"F1.wireOp",EDGE,"E202.trimOffspring"),sQuery(id+"F1.wireOp",EDGE,"E203.filletArc"),sQuery(id+"F1.wireOp",EDGE,"E204.filletArc"),sQuery(id+"F1.wireOp",EDGE,"E205.filletArc"),sQuery(id+"F1.wireOp",EDGE,"E206.filletArc"),sQuery(id+"F1.wireOp",EDGE,"E207.filletArc"),sQuery(id+"F1.wireOp",EDGE,"E208.filletArc"),sQuery(id+"F1.wireOp",EDGE,"E209.filletArc"),sQuery(id+"F1.wireOp",EDGE,"E210.filletArc"),sQuery(id+"F1.wireOp",EDGE,"E211.filletArc"),sQuery(id+"F1.wireOp",EDGE,"E212.filletArc"),sQuery(id+"F1.wireOp",EDGE,"E213.filletArc"),sQuery(id+"F1.wireOp",EDGE,"E214.filletArc"),sQuery(id+"F1.wireOp",EDGE,"E215.filletArc"),sQuery(id+"F1.wireOp",EDGE,"E216.filletArc"),sQuery(id+"F1.wireOp",EDGE,"E217.filletArc"),sQuery(id+"F1.wireOp",EDGE,"E218.filletArc"),sQuery(id+"F1.wireOp",EDGE,"E219.filletArc"),sQuery(id+"F1.wireOp",EDGE,"E220.filletArc"),sQuery(id+"F1.wireOp",EDGE,"E221.filletArc"),sQuery(id+"F1.wireOp",EDGE,"E222.filletArc"),sQuery(id+"F1.wireOp",EDGE,"E223.filletArc"),sQuery(id+"F1.wireOp",EDGE,"E224.filletArc"),sQuery(id+"F1.wireOp",EDGE,"E225.filletArc"),sQuery(id+"F1.wireOp",EDGE,"E226.filletArc"),sQuery(id+"F1.wireOp",EDGE,"E227.filletArc"),sQuery(id+"F1.wireOp",EDGE,"E228.filletArc"),sQuery(id+"F1.wireOp",EDGE,"E229.filletArc"),sQuery(id+"F1.wireOp",EDGE,"E230.filletArc"),sQuery(id+"F1.wireOp",EDGE,"E231.filletArc"),sQuery(id+"F1.wireOp",EDGE,"E232.filletArc"),sQuery(id+"F1.wireOp",EDGE,"E233.filletArc"),sQuery(id+"F1.wireOp",EDGE,"E234.filletArc"),sQuery(id+"F1.wireOp",EDGE,"E235.filletArc"),sQuery(id+"F1.wireOp",EDGE,"E236.filletArc"),sQuery(id+"F1.wireOp",EDGE,"E237.filletArc"),sQuery(id+"F1.wireOp",EDGE,"E238.filletArc"),sQuery(id+"F1.wireOp",EDGE,"E239.filletArc")])],"isStart":true});
            var sketch = newSketch(context, id + "F3", { "sketchPlane" : qUnion([Q0])});
            skCircle(sketch, "E240", {"center": v(-7.55, 23) * mm, "radius": 3 * mm});
            skCircle(sketch, "E241", {"center": v(7.55, 23) * mm, "radius": 3 * mm});
            skCircle(sketch, "E242", {"center": v(-7.55, -23) * mm, "radius": 3 * mm});
            skCircle(sketch, "E243", {"center": v(7.55, -23) * mm, "radius": 3 * mm});
            skSolve(sketch);
        }
        {
            var Q0;
            {var subQ0=sQuery(id+"F3.wireOp",EDGE,"E240");var subQ1=makeQuery(id+"F3.imprint","INTERSECT",VERTEX,{"derivedFrom":[makeQuery(id+"F2.opExtrude","CAP_EDGE",EDGE,{"disambiguationData":[OSD([sQuery(id+"F1.wireOp",EDGE,"E211.filletArc")])],"isStart":true}),subQ0]});var subQ2=makeQuery(id+"F3.imprint","INTERSECT",VERTEX,{"derivedFrom":[makeQuery(id+"F2.opExtrude","CAP_EDGE",EDGE,{"disambiguationData":[OSD([sQuery(id+"F1.wireOp",EDGE,"E214.filletArc")])],"isStart":true}),subQ0]});Q0=makeQuery(id+"F3.imprint","IMPRINT",FACE,{"disambiguationData":[TD([[makeQuery(id+"F3.imprint","IMPRINT",EDGE,{"disambiguationData":[TD([[subQ1,-1.0],[subQ2,1.0]])],"derivedFrom":subQ0}),-1.0]])]});}
            var Q1;
            {var subQ0=sQuery(id+"F3.wireOp",EDGE,"E241");var subQ1=makeQuery(id+"F3.imprint","INTERSECT",VERTEX,{"derivedFrom":[makeQuery(id+"F2.opExtrude","CAP_EDGE",EDGE,{"disambiguationData":[OSD([sQuery(id+"F1.wireOp",EDGE,"E217.filletArc")])],"isStart":true}),subQ0]});var subQ2=makeQuery(id+"F3.imprint","INTERSECT",VERTEX,{"derivedFrom":[makeQuery(id+"F2.opExtrude","CAP_EDGE",EDGE,{"disambiguationData":[OSD([sQuery(id+"F1.wireOp",EDGE,"E215.filletArc")])],"isStart":true}),subQ0]});Q1=makeQuery(id+"F3.imprint","IMPRINT",FACE,{"disambiguationData":[TD([[makeQuery(id+"F3.imprint","IMPRINT",EDGE,{"disambiguationData":[TD([[subQ1,-1.0],[subQ2,1.0]])],"derivedFrom":subQ0}),-1.0]])]});}
            var Q2;
            {var subQ0=sQuery(id+"F3.wireOp",EDGE,"E243");var subQ1=makeQuery(id+"F3.imprint","INTERSECT",VERTEX,{"derivedFrom":[makeQuery(id+"F2.opExtrude","CAP_EDGE",EDGE,{"disambiguationData":[OSD([sQuery(id+"F1.wireOp",EDGE,"E209.filletArc")])],"isStart":true}),subQ0]});var subQ2=makeQuery(id+"F3.imprint","INTERSECT",VERTEX,{"derivedFrom":[makeQuery(id+"F2.opExtrude","CAP_EDGE",EDGE,{"disambiguationData":[OSD([sQuery(id+"F1.wireOp",EDGE,"E208.filletArc")])],"isStart":true}),subQ0]});Q2=makeQuery(id+"F3.imprint","IMPRINT",FACE,{"disambiguationData":[TD([[makeQuery(id+"F3.imprint","IMPRINT",EDGE,{"disambiguationData":[TD([[subQ1,-1.0],[subQ2,1.0]])],"derivedFrom":subQ0}),-1.0]])]});}
            var Q3;
            {var subQ0=sQuery(id+"F3.wireOp",EDGE,"E242");var subQ1=makeQuery(id+"F3.imprint","INTERSECT",VERTEX,{"derivedFrom":[makeQuery(id+"F2.opExtrude","CAP_EDGE",EDGE,{"disambiguationData":[OSD([sQuery(id+"F1.wireOp",EDGE,"E204.filletArc")])],"isStart":true}),subQ0]});var subQ2=makeQuery(id+"F3.imprint","INTERSECT",VERTEX,{"derivedFrom":[makeQuery(id+"F2.opExtrude","CAP_EDGE",EDGE,{"disambiguationData":[OSD([sQuery(id+"F1.wireOp",EDGE,"E203.filletArc")])],"isStart":true}),subQ0]});Q3=makeQuery(id+"F3.imprint","IMPRINT",FACE,{"disambiguationData":[TD([[makeQuery(id+"F3.imprint","IMPRINT",EDGE,{"disambiguationData":[TD([[subQ1,-1.0],[subQ2,1.0]])],"derivedFrom":subQ0}),-1.0]])]});}
            extrude(context, id + "F4", {"entities" : qUnion([Q0, Q1, Q2, Q3]), "depth" : 4 * mm, "offsetDistance" : 25 * mm});
        }
        {
            var Q0;
            Q0=makeQuery(id+"F4.opExtrude","CAP_FACE",FACE,{"disambiguationData":[OSD([sQuery(id+"F3.wireOp",EDGE,"E240")])],"isStart":false});
            var sketch = newSketch(context, id + "F5", { "sketchPlane" : qUnion([Q0])});
            skLineSegment(sketch, "E244.0.0", {"start": v(15, 27.5) * mm, "end": v(15, -27.5) * mm});
            skLineSegment(sketch, "E244.0.1", {"start": v(15, -27.5) * mm, "end": v(-15, -27.5) * mm});
            skLineSegment(sketch, "E244.0.2", {"start": v(-15, -27.5) * mm, "end": v(-15, 27.5) * mm});
            skLineSegment(sketch, "E244.0.3", {"start": v(-15, 27.5) * mm, "end": v(15, 27.5) * mm});
            skSolve(sketch);
        }
        {
            var Q0;
            Q0=makeQuery(id+"F5.imprint","IMPRINT",FACE,{"disambiguationData":[TD([[makeQuery(id+"F5.imprint","IMPRINT",EDGE,{"derivedFrom":sQuery(id+"F5.wireOp",EDGE,"E244.0.0")}),-1.0]])]});
            var Q1;
            Q1=makeQuery(id+"F5.imprint","IMPRINT",FACE,{"disambiguationData":[TD([[makeQuery(id+"F5.imprint","IMPRINT",EDGE,{"derivedFrom":makeQuery(id+"F4.opExtrude","CAP_EDGE",EDGE,{"disambiguationData":[OSD([sQuery(id+"F3.wireOp",EDGE,"E240")])],"isStart":false})}),-1.0]])]});
            extrude(context, id + "F6", {"entities" : qUnion([Q0, Q1]), "depth" : 10 * mm, "offsetDistance" : 25 * mm});
        }
    });
